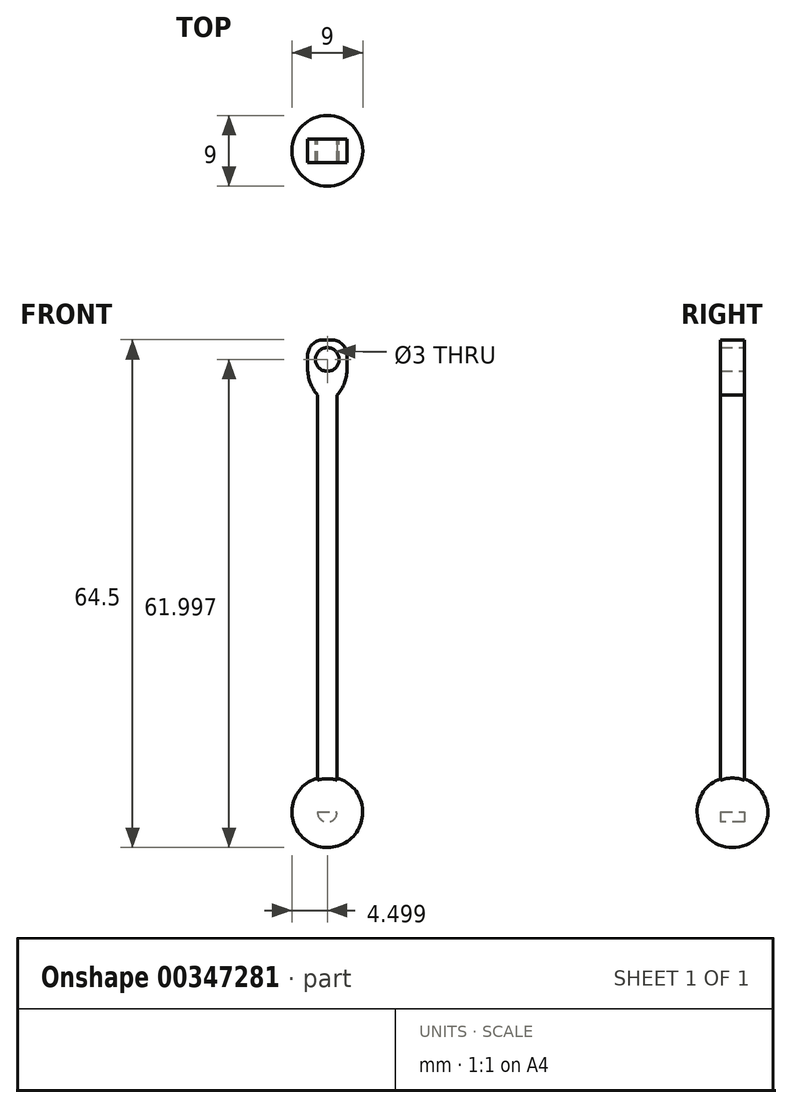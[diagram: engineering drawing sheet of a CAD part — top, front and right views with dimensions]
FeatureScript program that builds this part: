
annotation { "Feature Type Name" : "Feature", "Feature Type Description" : "" }
export const myFeature = defineFeature(function(context is Context, id is Id, definition is map)
    precondition{}
    {
        {
            var Q0;
            Q0=qCreatedBy(makeId("Front.planeOp"),FACE);
            var sketch = newSketch(context, id + "F0", { "sketchPlane" : qUnion([Q0])});
            skLineSegment(sketch, "E0.bottom", {"start": v(-19.95, 50.14) * mm, "end": v(-14.95, 50.14) * mm});
            skLineSegment(sketch, "E0.left", {"start": v(-19.95, 50.14) * mm, "end": v(-19.95, 43.14) * mm});
            skLineSegment(sketch, "E0.right", {"start": v(-14.95, 50.14) * mm, "end": v(-14.95, 43.14) * mm});
            skCircle(sketch, "E1", {"center": v(-17.45, 47.64) * mm, "radius": 1.5 * mm});
            skLineSegment(sketch, "E2", {"start": v(-17.45, -9.86) * mm, "end": v(-16.2, -9.86) * mm});
            skLineSegment(sketch, "E3", {"start": v(-18.7, 10.14) * mm, "end": v(-18.7, 43.14) * mm});
            skLineSegment(sketch, "E4", {"start": v(-18.7, 43.14) * mm, "end": v(-19.95, 43.14) * mm});
            skLineSegment(sketch, "E5", {"start": v(-16.2, 10.14) * mm, "end": v(-16.2, 43.14) * mm});
            skLineSegment(sketch, "E6", {"start": v(-16.2, 43.14) * mm, "end": v(-14.95, 43.14) * mm});
            skLineSegment(sketch, "E7", {"start": v(-18.7, -9.86) * mm, "end": v(-17.45, -9.86) * mm});
            skLineSegment(sketch, "E8", {"start": v(-16.2, 10.14) * mm, "end": v(-16.2, -9.86) * mm});
            skLineSegment(sketch, "E9", {"start": v(-18.7, 10.14) * mm, "end": v(-18.7, -9.86) * mm});
            skSolve(sketch);
        }
        {
            var Q0;
            Q0 = qSketchRegion(id + "F0", true);
            extrude(context, id + "F1", {"entities" : qUnion([Q0]), "depth" : 3 * mm});
        }
        {
            var Q0;
            Q0=makeQuery(id+"F1.opExtrude","SWEPT_EDGE",EDGE,{"disambiguationData":[OSD([sQuery(id+"F0.wireOp",EDGE,"E0.bottom"),sQuery(id+"F0.wireOp",EDGE,"E0.right")])]});
            fillet(context, id + "F2", {"entities" : qUnion([Q0]), "radius" : 2 * mm, "tangentPropagation" : true, "allowEdgeOverflow" : false});
        }
        {
            var Q0;
            Q0=makeQuery(id+"F1.opExtrude","SWEPT_EDGE",EDGE,{"disambiguationData":[OSD([sQuery(id+"F0.wireOp",EDGE,"E0.bottom"),sQuery(id+"F0.wireOp",EDGE,"E0.left")])]});
            fillet(context, id + "F3", {"entities" : qUnion([Q0]), "radius" : 2 * mm, "tangentPropagation" : true, "allowEdgeOverflow" : false});
        }
        {
            var Q0;
            Q0=makeQuery(id+"F1.opExtrude","SWEPT_EDGE",EDGE,{"disambiguationData":[OSD([sQuery(id+"F0.wireOp",EDGE,"E0.right"),sQuery(id+"F0.wireOp",EDGE,"E6")])]});
            var Q1;
            Q1=makeQuery(id+"F1.opExtrude","SWEPT_EDGE",EDGE,{"disambiguationData":[OSD([sQuery(id+"F0.wireOp",EDGE,"E0.left"),sQuery(id+"F0.wireOp",EDGE,"E4")])]});
            fillet(context, id + "F4", {"entities" : qUnion([Q0, Q1]), "radius" : 5 * mm, "tangentPropagation" : true, "allowEdgeOverflow" : false});
        }
        {
            var Q0;
            Q0=makeQuery(id+"F1.opExtrude","SWEPT_FACE",FACE,{"disambiguationData":[OSD([sQuery(id+"F0.wireOp",EDGE,"E2"),sQuery(id+"F0.wireOp",EDGE,"E7")])]});
            var sketch = newSketch(context, id + "F5", { "sketchPlane" : qUnion([Q0])});
            skLineSegment(sketch, "E10", {"start": v(-17.45, 3) * mm, "end": v(-17.45, 0) * mm, "construction": true});
            skLineSegment(sketch, "E11", {"start": v(-17.45, 6) * mm, "end": v(-17.45, -3) * mm});
            skArc(sketch, "E12", {"start": v(-17.45, 6) * mm, "mid": v(-21.95, 1.5) * mm, "end": v(-17.45, -3) * mm});
            skSolve(sketch);
        }
        {
            var Q0;
            {var subQ0=sQuery(id+"F5.wireOp",EDGE,"E12");Q0=makeQuery(id+"F5.imprint","IMPRINT",FACE,{"disambiguationData":[TD([[makeQuery(id+"F5.imprint","IMPRINT",EDGE,{"derivedFrom":subQ0}),1.0]])]});}
            var Q1;
            Q1=sQuery(id+"F5.wireOp",EDGE,"E11");
            revolve(context, id + "F6", {"operationType" : NewBodyOperationType.ADD, "entities" : qUnion([Q0]), "axis" : qUnion([Q1]), "revolveType" : RevolveType.FULL});
        }
    });
